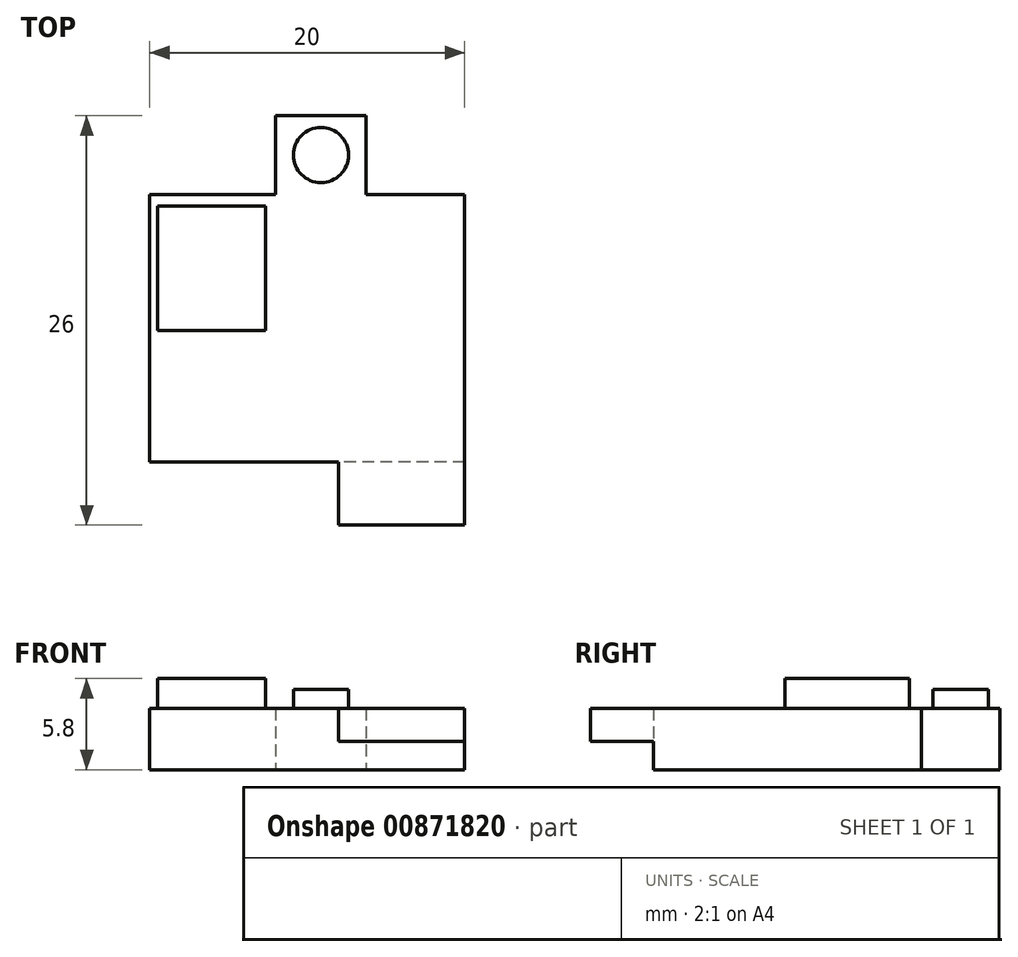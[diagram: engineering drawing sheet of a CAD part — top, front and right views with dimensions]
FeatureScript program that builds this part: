
annotation { "Feature Type Name" : "Feature", "Feature Type Description" : "" }
export const myFeature = defineFeature(function(context is Context, id is Id, definition is map)
    precondition{}
    {
        {
            var Q0;
            Q0=qCreatedBy(makeId("Top.planeOp"),FACE);
            var sketch = newSketch(context, id + "F0", { "sketchPlane" : qUnion([Q0])});
            skLineSegment(sketch, "E0.bottom", {"start": v(10, 8.5) * mm, "end": v(3.75, 8.5) * mm});
            skLineSegment(sketch, "E0.top", {"start": v(10, -8.5) * mm, "end": v(-10, -8.5) * mm});
            skLineSegment(sketch, "E0.left", {"start": v(10, 8.5) * mm, "end": v(10, -8.5) * mm});
            skLineSegment(sketch, "E0.right", {"start": v(-10, 8.5) * mm, "end": v(-10, -8.5) * mm});
            skPoint(sketch, "E0.middle", {"position": v(0, 0) * mm});
            skLineSegment(sketch, "E1.top", {"start": v(-2, 13.5) * mm, "end": v(3.75, 13.5) * mm});
            skLineSegment(sketch, "E1.left", {"start": v(-2, 8.5) * mm, "end": v(-2, 13.5) * mm});
            skLineSegment(sketch, "E1.right", {"start": v(3.75, 8.5) * mm, "end": v(3.75, 13.5) * mm});
            skLineSegment(sketch, "E2.trimOffspring", {"start": v(-2, 8.5) * mm, "end": v(-10, 8.5) * mm});
            skSolve(sketch);
        }
        {
            var Q0;
            Q0=makeQuery(id+"F0.imprint","IMPRINT",FACE,{"disambiguationData":[TD([[makeQuery(id+"F0.imprint","IMPRINT",EDGE,{"derivedFrom":sQuery(id+"F0.wireOp",EDGE,"E0.bottom")}),1.0]])]});
            extrude(context, id + "F1", {"entities" : qUnion([Q0]), "depth" : 2.1 * mm, "offsetDistance" : 25 * mm, "hasSecondDirection" : true, "secondDirectionOppositeDirection" : true, "secondDirectionDepth" : 1.8 * mm});
        }
        {
            var Q0;
            Q0=qCreatedBy(makeId("Top.planeOp"),FACE);
            var sketch = newSketch(context, id + "F2", { "sketchPlane" : qUnion([Q0])});
            skPoint(sketch, "E3.0", {"position": v(-2, 8.5) * mm});
            skPoint(sketch, "E4.0", {"position": v(3.75, 13.5) * mm});
            skLineSegment(sketch, "E5", {"start": v(-2, 8.5) * mm, "end": v(3.75, 13.5) * mm, "construction": true});
            skCircle(sketch, "E6", {"center": v(0.88, 11) * mm, "radius": 1.75 * mm});
            skSolve(sketch);
        }
        {
            var Q0;
            Q0=qSketchRegion(id+"F2",true);
            extrude(context, id + "F3", {"entities" : qUnion([Q0]), "operationType" : NewBodyOperationType.ADD, "depth" : 3.3 * mm, "offsetDistance" : 25 * mm});
        }
        {
            var Q0;
            Q0=qCreatedBy(makeId("Top.planeOp"),FACE);
            var sketch = newSketch(context, id + "F4", { "sketchPlane" : qUnion([Q0])});
            skLineSegment(sketch, "E7.0", {"start": v(-10, 8.5) * mm, "end": v(-10, -8.5) * mm, "construction": true});
            skLineSegment(sketch, "E8.0", {"start": v(-2, 8.5) * mm, "end": v(-10, 8.5) * mm, "construction": true});
            skLineSegment(sketch, "E9.bottom", {"start": v(-9.5, 7.75) * mm, "end": v(-2.65, 7.75) * mm});
            skLineSegment(sketch, "E9.top", {"start": v(-9.5, -0.15) * mm, "end": v(-2.65, -0.15) * mm});
            skLineSegment(sketch, "E9.left", {"start": v(-9.5, 7.75) * mm, "end": v(-9.5, -0.15) * mm});
            skLineSegment(sketch, "E9.right", {"start": v(-2.65, 7.75) * mm, "end": v(-2.65, -0.15) * mm});
            skSolve(sketch);
        }
        {
            var Q0;
            Q0=qSketchRegion(id+"F4",true);
            extrude(context, id + "F5", {"entities" : qUnion([Q0]), "operationType" : NewBodyOperationType.ADD, "depth" : 4 * mm, "offsetDistance" : 25 * mm});
        }
        {
            var Q0;
            Q0=makeQuery(id+"F1.opExtrude","SWEPT_FACE",FACE,{"disambiguationData":[OSD([sQuery(id+"F0.wireOp",EDGE,"E0.top")])]});
            var sketch = newSketch(context, id + "F6", { "sketchPlane" : qUnion([Q0])});
            skLineSegment(sketch, "E10.bottom", {"start": v(10, 2.1) * mm, "end": v(2, 2.1) * mm});
            skLineSegment(sketch, "E10.top", {"start": v(10, 0) * mm, "end": v(2, 0) * mm});
            skLineSegment(sketch, "E10.left", {"start": v(10, 2.1) * mm, "end": v(10, 0) * mm});
            skLineSegment(sketch, "E10.right", {"start": v(2, 2.1) * mm, "end": v(2, 0) * mm});
            skSolve(sketch);
        }
        {
            var Q0;
            Q0=qSketchRegion(id+"F6",true);
            extrude(context, id + "F7", {"entities" : qUnion([Q0]), "operationType" : NewBodyOperationType.ADD, "depth" : 4 * mm, "offsetDistance" : 25 * mm});
        }
    });
